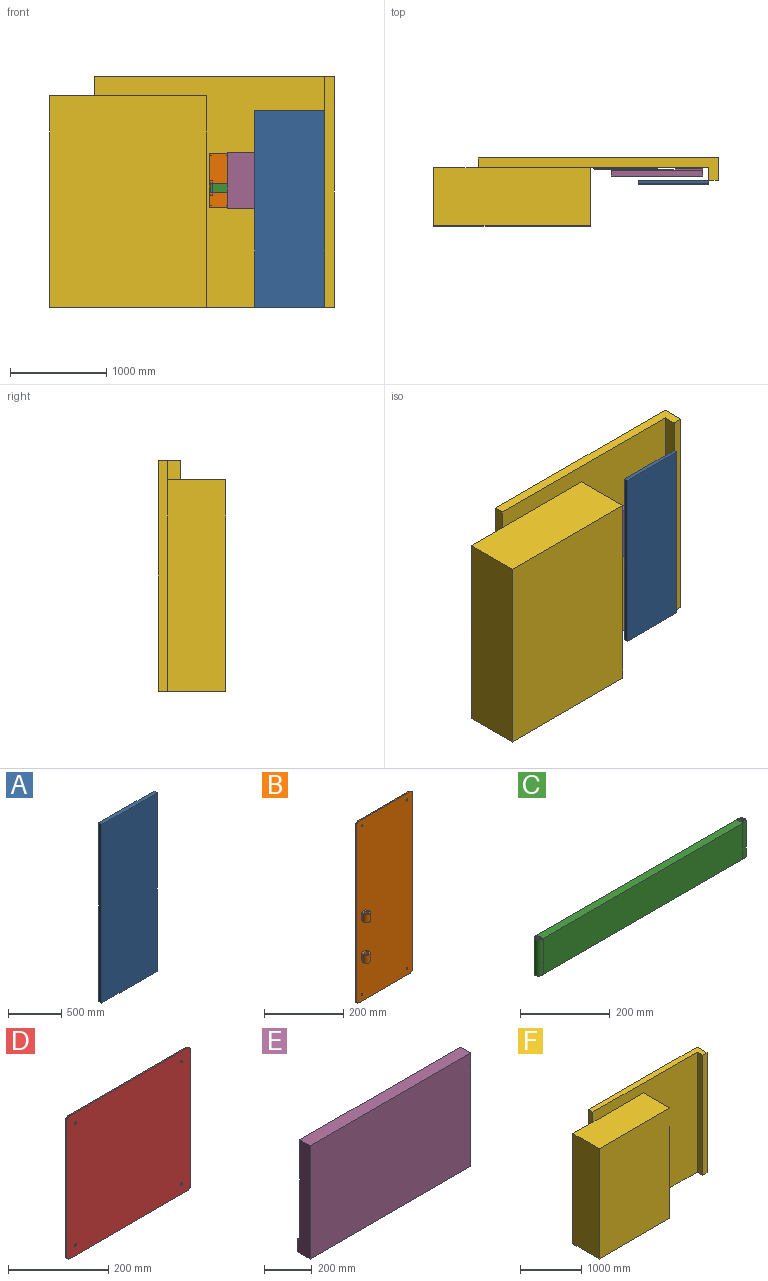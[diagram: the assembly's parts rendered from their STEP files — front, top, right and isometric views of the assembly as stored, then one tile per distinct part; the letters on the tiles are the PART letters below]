
ASSEMBLY  parts=6 mates=5
PART A: 6 faces, bbox 730x40x2050 mm
  f0: plane 2050x730mm, normal (0,1,0), area 1496500mm2, adj f1,f3,f4,f5
  f1: plane 2050x40mm, normal (1,0,0), area 82000mm2, adj f0,f2,f4,f5
  f2: plane 2050x730mm, normal (0,-1,0), area 1496500mm2, adj f1,f3,f4,f5
  f3: plane 2050x40mm, normal (-1,0,0), area 82000mm2, adj f0,f2,f4,f5
  f4: plane 730x40mm, normal (0,0,1), area 29200mm2, adj f0,f1,f2,f3
  f5: plane 730x40mm, normal (0,0,-1), area 29200mm2, adj f0,f1,f2,f3
PART B: 27 faces, bbox 200x23x560 mm
  f0: plane 540x3mm, normal (-1,0,0), area 1620mm2, adj f1,f11,f12,f13
  f1: cylinder r=10mm len=10mm, axis (0,-1,0), area 47.1mm2, adj f0,f2,f12,f13
  f2: plane 180x3mm, normal (0,0,1), area 540mm2, adj f1,f3,f12,f13
  f3: cylinder r=10mm len=10mm, axis (0,-1,0), area 47.1mm2, adj f2,f4,f12,f13
  f4: plane 540x3mm, normal (1,0,0), area 1620mm2, adj f3,f5,f12,f13
  f5: cylinder r=10mm len=10mm, axis (0,-1,0), area 47.1mm2, adj f4,f6,f12,f13
  f6: plane 180x3mm, normal (0,0,-1), area 540mm2, adj f5,f11,f12,f13
  f7: cylinder r=3mm len=6mm, axis (0,-1,0), area 56.5mm2, adj f12,f13
  f8: cylinder r=3mm len=6mm, axis (0,-1,0), area 56.5mm2, adj f12,f13
  f9: cylinder r=3mm len=6mm, axis (0,-1,0), area 56.5mm2, adj f12,f13
  f10: cylinder r=3mm len=6mm, axis (0,-1,0), area 56.5mm2, adj f12,f13
  f11: cylinder r=10mm len=10mm, axis (0,-1,0), area 47.1mm2, adj f0,f6,f12,f13
  f12: plane 560x200mm, normal (0,1,0), area 111801.1mm2, adj f0,f1,f2,f3,f4,f5,f6,f7
  f13: plane 560x200mm, normal (0,-1,0), area 111051.1mm2, adj f0,f1,f2,f3,f4,f5,f6,f7
  f14: plane 20x20mm, normal (0,0,1), area 216.6mm2, adj f13,f15,f17,f18,f19
  f15: plane 25x3.39mm, normal (-1,0,0), area 84.6mm2, adj f13,f14,f16,f18
  f16: plane 20x20mm, normal (0,0,-1), area 216.6mm2, adj f13,f15,f17,f18,f19
  f17: plane 25x3.39mm, normal (1,0,0), area 84.6mm2, adj f13,f14,f16,f18
  f18: cylinder r=10mm len=25mm, axis (0,0,1), area 1146.8mm2, adj f14,f15,f16,f17
  f19: cylinder r=6mm len=25mm, axis (0,0,1), area 942.5mm2, adj f14,f16
  f20: plane 20x20mm, normal (0,0,-1), area 329.7mm2, adj f13,f21,f23,f24
  f21: plane 25x3.39mm, normal (-1,0,0), area 84.6mm2, adj f13,f20,f22,f24
  f22: plane 20x20mm, normal (0,0,1), area 216.6mm2, adj f13,f21,f23,f24,f25
  f23: plane 25x3.39mm, normal (1,0,0), area 84.6mm2, adj f13,f20,f22,f24
  f24: cylinder r=10mm len=25mm, axis (0,0,-1), area 1146.8mm2, adj f20,f21,f22,f23
  f25: cylinder r=6mm len=20mm, axis (0,0,1), area 754mm2, adj f22,f26
  f26: plane 12x12mm, normal (0,0,1), area 113.1mm2, adj f25
PART C: 12 faces, bbox 660x20x98 mm
  f0: plane 98x2mm, normal (-1,0,0), area 196mm2, adj f1,f2,f9,f10
  f1: plane 660x20mm, normal (0,0,1), area 12872.7mm2, adj f0,f3,f4,f5,f6,f7,f8,f9
  f2: plane 660x20mm, normal (0,0,-1), area 12872.7mm2, adj f0,f3,f4,f5,f6,f7,f8,f9
  f3: cylinder r=10mm len=98mm, axis (0,0,-1), area 4340mm2, adj f1,f2,f5,f6
  f4: cylinder r=6mm len=98mm, axis (0,0,-1), area 3694.5mm2, adj f1,f2
  f5: plane 98x2mm, normal (1,0,0), area 196mm2, adj f1,f2,f3,f8
  f6: plane 98x2mm, normal (1,0,0), area 196mm2, adj f1,f2,f3,f9
  f7: plane 98x2mm, normal (-1,0,0), area 196mm2, adj f1,f2,f8,f10
  f8: plane 628x98mm, normal (0,1,0), area 61544mm2, adj f1,f2,f5,f7
  f9: plane 628x98mm, normal (0,-1,0), area 61544mm2, adj f0,f1,f2,f6
  f10: cylinder r=10mm len=98mm, axis (0,0,-1), area 4340mm2, adj f0,f1,f2,f7
  f11: cylinder r=6mm len=98mm, axis (0,0,-1), area 3694.5mm2, adj f1,f2
PART D: 27 faces, bbox 350x23x350 mm
  f0: plane 330x3mm, normal (0,0,-1), area 990mm2, adj f1,f11,f12,f13
  f1: cylinder r=10mm len=10mm, axis (0,-1,0), area 47.1mm2, adj f0,f2,f12,f13
  f2: plane 330x3mm, normal (-1,0,0), area 990mm2, adj f1,f3,f12,f13
  f3: cylinder r=10mm len=10mm, axis (0,-1,0), area 47.1mm2, adj f2,f4,f12,f13
  f4: plane 330x3mm, normal (0,0,1), area 990mm2, adj f3,f5,f12,f13
  f5: cylinder r=10mm len=10mm, axis (0,-1,0), area 47.1mm2, adj f4,f6,f12,f13
  f6: plane 330x3mm, normal (1,0,0), area 990mm2, adj f5,f11,f12,f13
  f7: cylinder r=3mm len=6mm, axis (0,-1,0), area 56.5mm2, adj f12,f13
  f8: cylinder r=3mm len=6mm, axis (0,-1,0), area 56.5mm2, adj f12,f13
  f9: cylinder r=3mm len=6mm, axis (0,-1,0), area 56.5mm2, adj f12,f13
  f10: cylinder r=3mm len=6mm, axis (0,-1,0), area 56.5mm2, adj f12,f13
  f11: cylinder r=10mm len=10mm, axis (0,-1,0), area 47.1mm2, adj f0,f6,f12,f13
  f12: plane 350x350mm, normal (0,1,0), area 121551.1mm2, adj f0,f1,f2,f3,f4,f5,f6,f7
  f13: plane 350x350mm, normal (0,-1,0), area 122301.1mm2, adj f0,f1,f2,f3,f4,f5,f6,f7
  f14: cylinder r=10mm len=25mm, axis (0,0,-1), area 1146.8mm2, adj f15,f16,f19,f20
  f15: plane 20x20mm, normal (0,0,1), area 216.6mm2, adj f12,f14,f17,f19,f20
  f16: plane 20x20mm, normal (0,0,-1), area 329.7mm2, adj f12,f14,f19,f20
  f17: cylinder r=6mm len=20mm, axis (0,0,1), area 754mm2, adj f15,f18
  f18: plane 12x12mm, normal (0,0,1), area 113.1mm2, adj f17
  f19: plane 25x3.39mm, normal (1,0,0), area 84.6mm2, adj f12,f14,f15,f16
  f20: plane 25x3.39mm, normal (-1,0,0), area 84.6mm2, adj f12,f14,f15,f16
  f21: cylinder r=10mm len=25mm, axis (0,0,1), area 1146.8mm2, adj f22,f23,f25,f26
  f22: plane 20x20mm, normal (0,0,-1), area 216.6mm2, adj f12,f21,f24,f25,f26
  f23: plane 20x20mm, normal (0,0,1), area 216.6mm2, adj f12,f21,f24,f25,f26
  f24: cylinder r=6mm len=25mm, axis (0,0,1), area 942.5mm2, adj f22,f23
  f25: plane 25x3.39mm, normal (1,0,0), area 84.6mm2, adj f12,f21,f22,f23
  f26: plane 25x3.39mm, normal (-1,0,0), area 84.6mm2, adj f12,f21,f22,f23
PART E: 20 faces, bbox 950x76x580 mm
  f0: plane 950x61mm, normal (0,0,1), area 57950mm2, adj f1,f3,f4,f5
  f1: plane 580x76mm, normal (-1,0,0), area 36355mm2, adj f0,f2,f4,f5,f9,f11
  f2: plane 950x76mm, normal (0,0,-1), area 66500mm2, adj f1,f3,f4,f5,f7,f8,f10,f11
  f3: plane 580x76mm, normal (1,0,0), area 36355mm2, adj f0,f2,f4,f5,f6,f8
  f4: plane 950x580mm, normal (0,-1,0), area 551000mm2, adj f0,f1,f2,f3
  f5: plane 950x580mm, normal (0,1,0), area 513836.9mm2, adj f0,f1,f2,f3,f6,f7,f9,f10
  f6: plane 285x15mm, normal (0,0,1), area 4275mm2, adj f3,f5,f7,f8
  f7: plane 65x15mm, normal (-1,0,0), area 975mm2, adj f2,f5,f6,f8
  f8: plane 285x65mm, normal (0,1,0), area 18525mm2, adj f2,f3,f6,f7
  f9: plane 285x15mm, normal (0,0,1), area 4275mm2, adj f1,f5,f10,f11
  f10: plane 65x15mm, normal (1,0,0), area 975mm2, adj f2,f5,f9,f11
  f11: plane 285x65mm, normal (0,1,0), area 18525mm2, adj f1,f2,f9,f10
  f12: cylinder r=3mm len=15mm, axis (0,1,0), area 282.7mm2, adj f5,f13
  f13: plane 6x6mm, normal (0,1,0), area 28.3mm2, adj f12
  f14: cylinder r=3mm len=15mm, axis (0,1,0), area 282.7mm2, adj f5,f15
  f15: plane 6x6mm, normal (0,1,0), area 28.3mm2, adj f14
  f16: cylinder r=3mm len=15mm, axis (0,1,0), area 282.7mm2, adj f5,f17
  f17: plane 6x6mm, normal (0,1,0), area 28.3mm2, adj f16
  f18: cylinder r=3mm len=15mm, axis (0,1,0), area 282.7mm2, adj f5,f19
  f19: plane 6x6mm, normal (0,1,0), area 28.3mm2, adj f18
PART F: 13 faces, bbox 2961.4x705x2400 mm
  f0: plane 2961.41x705mm, normal (0,0,-1), area 1250001.1mm2, adj f2,f3,f4,f5,f6,f7,f8,f9
  f1: plane 2500x230mm, normal (0,0,1), area 263000mm2, adj f2,f3,f4,f5,f6,f7
  f2: plane 2400x100mm, normal (-1,0,0), area 240000mm2, adj f0,f1,f3,f4,f8
  f3: plane 2500x2400mm, normal (0,1,0), area 6000000mm2, adj f0,f1,f2,f6
  f4: plane 2400x2400mm, normal (0,-1,0), area 3186000mm2, adj f0,f1,f2,f7,f9,f12
  f5: plane 2400x100mm, normal (0,-1,0), area 240000mm2, adj f0,f1,f6,f7
  f6: plane 2400x230mm, normal (1,0,0), area 552000mm2, adj f0,f1,f3,f5
  f7: plane 2400x130mm, normal (-1,0,0), area 312000mm2, adj f0,f1,f4,f5
  f8: plane 2200x461.41mm, normal (0,1,0), area 1015094.8mm2, adj f0,f2,f11,f12
  f9: plane 2200x605mm, normal (1,0,0), area 1331000mm2, adj f0,f4,f10,f12
  f10: plane 2200x1631.41mm, normal (0,-1,0), area 3589094.8mm2, adj f0,f9,f11,f12
  f11: plane 2200x605mm, normal (-1,0,0), area 1331000mm2, adj f0,f8,f10,f12
  f12: plane 1631.41x605mm, normal (0,0,1), area 987001.1mm2, adj f4,f8,f9,f10,f11
PLACE A rot(axis=(0,0,1),0deg) t=(0,0,0)mm
PLACE B t=(-537.14,-26,1320.79)mm
PLACE C t=(-537.14,-26,1320.79)mm
PLACE D rot(axis=(0,0,-1),0deg) t=(-537.14,-26,1320.79)mm
PLACE E rot(axis=(0,0,-1),0deg) t=(-537.14,-26,1320.79)mm
PLACE F at identity fixed
MATE revolute C.f4 <-> D.f14  axis (0,0,-1) through (-537.14,-13,1190.79)mm
MATE revolute C.f10 <-> B.f18  axis (0,0,-1) through (-1177.14,-13,1190.79)mm
MATE fastened F.f4 <-> B.f7  axis (0,-1,0) through (-1183.14,0,1580.79)mm
MATE revolute A.f5 <-> F.f0  axis (0,0,-1) through (0,-130,0)mm
MATE fastened E.f16 <-> D.f8  axis (0,1,0) through (-687.14,-26,1390.79)mm
